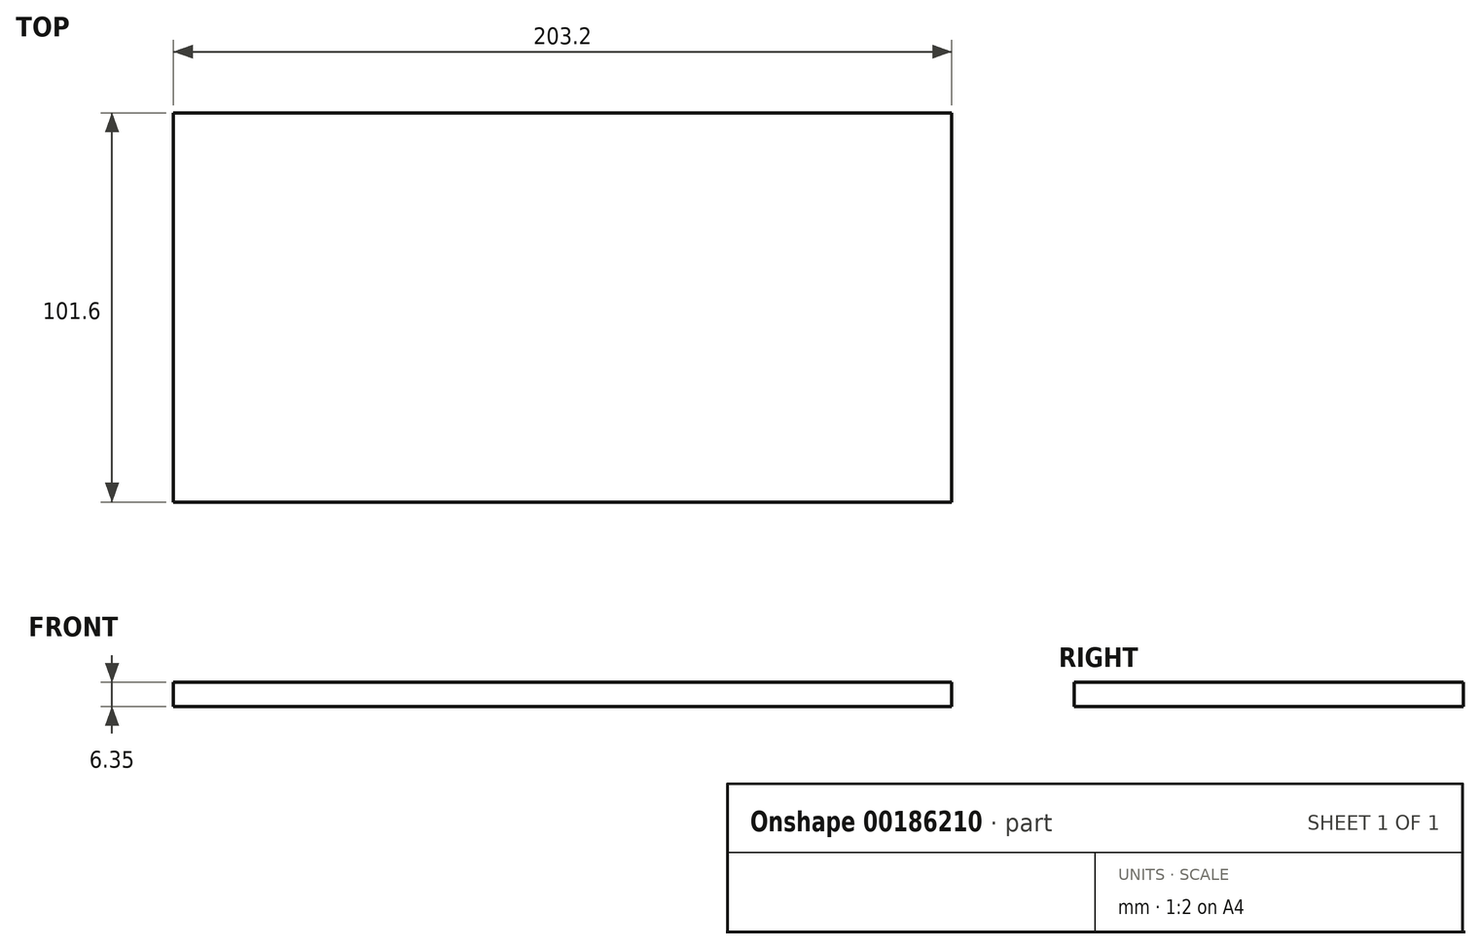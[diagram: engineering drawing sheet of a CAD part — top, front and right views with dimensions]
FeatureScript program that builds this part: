
annotation { "Feature Type Name" : "Feature", "Feature Type Description" : "" }
export const myFeature = defineFeature(function(context is Context, id is Id, definition is map)
    precondition{}
    {
        {
            var Q0;
            Q0=qCreatedBy(makeId("Top.planeOp"),FACE);
            var sketch = newSketch(context, id + "F0", { "sketchPlane" : qUnion([Q0])});
            skLineSegment(sketch, "E0.bottom", {"start": v(101.6, 50.8) * mm, "end": v(-101.6, 50.8) * mm});
            skLineSegment(sketch, "E0.top", {"start": v(101.6, -50.8) * mm, "end": v(-101.6, -50.8) * mm});
            skLineSegment(sketch, "E0.left", {"start": v(101.6, 50.8) * mm, "end": v(101.6, -50.8) * mm});
            skLineSegment(sketch, "E0.right", {"start": v(-101.6, 50.8) * mm, "end": v(-101.6, -50.8) * mm});
            skPoint(sketch, "E0.middle", {"position": v(0, 0) * mm});
            skSolve(sketch);
        }
        {
            var Q0;
            Q0 = qSketchRegion(id + "F0", true);
            extrude(context, id + "F1", {"entities" : qUnion([Q0]), "depth" : 6.35 * mm});
        }
    });
